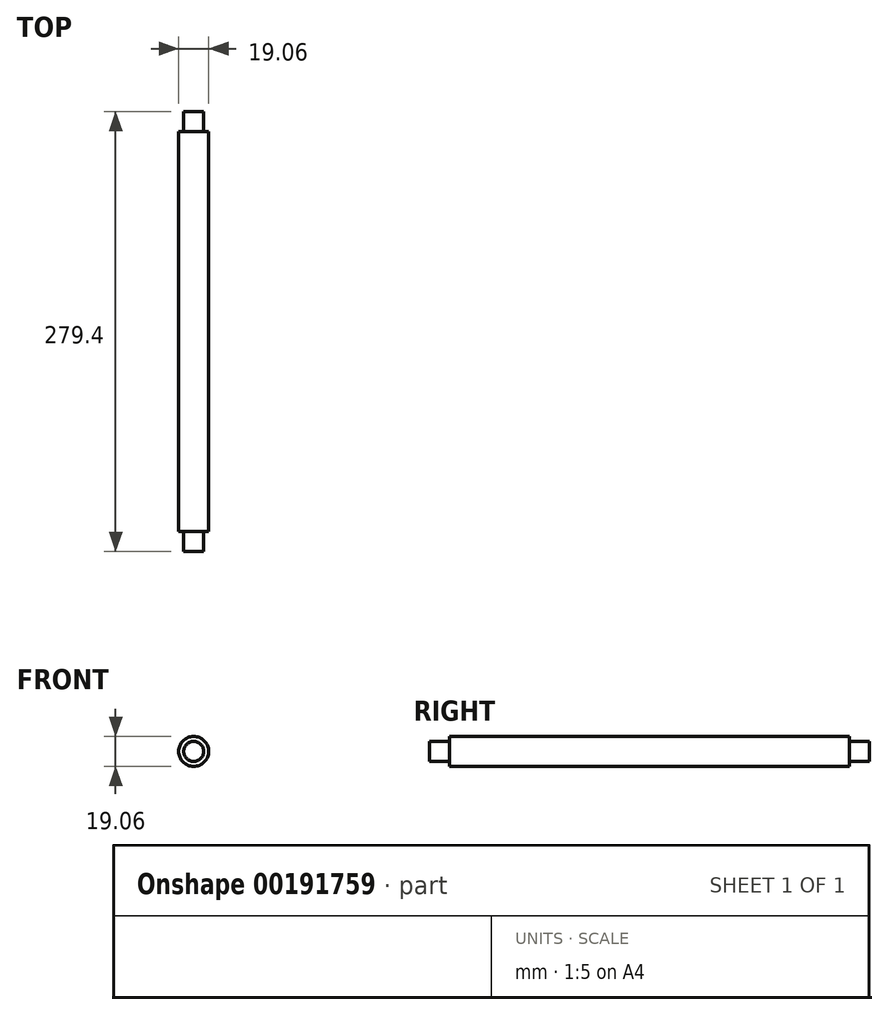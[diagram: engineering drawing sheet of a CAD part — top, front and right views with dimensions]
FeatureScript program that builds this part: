
annotation { "Feature Type Name" : "Feature", "Feature Type Description" : "" }
export const myFeature = defineFeature(function(context is Context, id is Id, definition is map)
    precondition{}
    {
        {
            var Q0;
            Q0=qCreatedBy(makeId("Front.planeOp"),FACE);
            var sketch = newSketch(context, id + "F0", { "sketchPlane" : qUnion([Q0])});
            skCircle(sketch, "E0", {"center": v(0, 0) * mm, "radius": 6.35 * mm});
            skSolve(sketch);
        }
        {
            var Q0;
            Q0 = qSketchRegion(id + "F0", true);
            extrude(context, id + "F1", {"entities" : qUnion([Q0]), "depth" : 12.7 * mm});
        }
        {
            var Q0;
            Q0=makeQuery(id+"F1.opExtrude","CAP_FACE",FACE,{"disambiguationData":[OSD([sQuery(id+"F0.wireOp",EDGE,"E0")])],"isStart":true});
            var sketch = newSketch(context, id + "F2", { "sketchPlane" : qUnion([Q0])});
            skCircle(sketch, "E1", {"center": v(0, 0) * mm, "radius": 9.53 * mm});
            skSolve(sketch);
        }
        {
            var Q0;
            Q0 = qSketchRegion(id + "F2", true);
            extrude(context, id + "F3", {"entities" : qUnion([Q0]), "operationType" : NewBodyOperationType.ADD, "depth" : 254 * mm});
        }
        {
            var Q0;
            Q0=makeQuery(id+"F3.opExtrude","CAP_FACE",FACE,{"disambiguationData":[OSD([sQuery(id+"F2.wireOp",EDGE,"E1")])],"isStart":false});
            var sketch = newSketch(context, id + "F4", { "sketchPlane" : qUnion([Q0])});
            skCircle(sketch, "E2", {"center": v(0, 0) * mm, "radius": 6.35 * mm});
            skSolve(sketch);
        }
        {
            var Q0;
            Q0=makeQuery(id+"F4.imprint","IMPRINT",FACE,{"disambiguationData":[TD([[makeQuery(id+"F4.imprint","IMPRINT",EDGE,{"derivedFrom":sQuery(id+"F4.wireOp",EDGE,"E2")}),1.0]])]});
            extrude(context, id + "F5", {"entities" : qUnion([Q0]), "operationType" : NewBodyOperationType.ADD, "depth" : 12.7 * mm});
        }
    });
